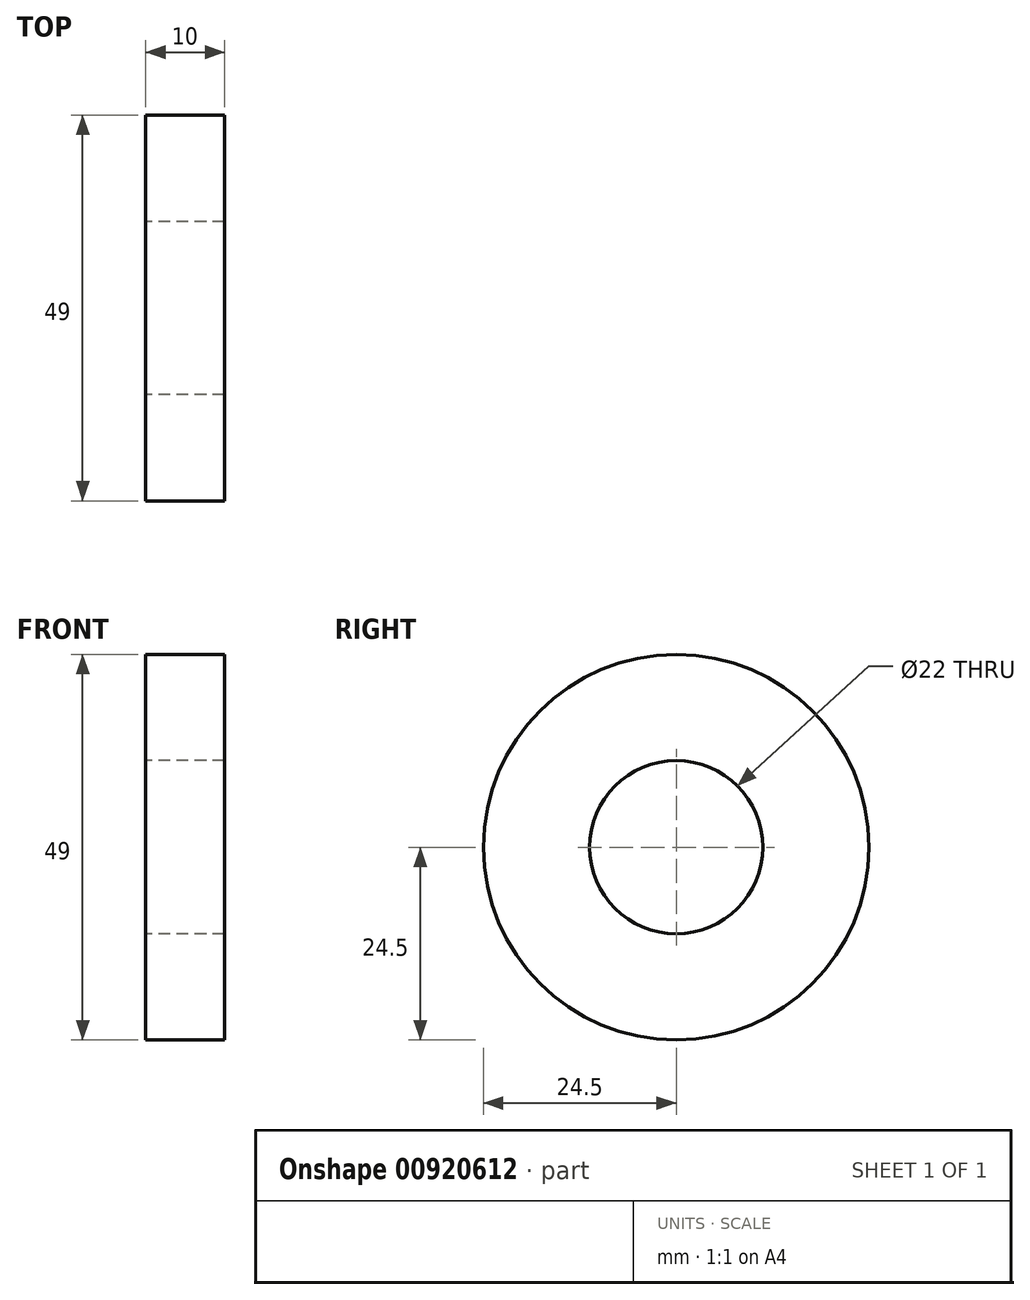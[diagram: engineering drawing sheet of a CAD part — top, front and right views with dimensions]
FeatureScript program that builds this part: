
annotation { "Feature Type Name" : "Feature", "Feature Type Description" : "" }
export const myFeature = defineFeature(function(context is Context, id is Id, definition is map)
    precondition{}
    {
        {
            var Q0;
            Q0=qCreatedBy(makeId("Front.planeOp"),FACE);
            var sketch = newSketch(context, id + "F0", { "sketchPlane" : qUnion([Q0])});
            skLineSegment(sketch, "E0", {"start": v(0, 0) * mm, "end": v(17.92, 0) * mm, "construction": true});
            skLineSegment(sketch, "E1.bottom", {"start": v(0, 11) * mm, "end": v(10, 11) * mm});
            skLineSegment(sketch, "E1.top", {"start": v(0, 24.5) * mm, "end": v(10, 24.5) * mm});
            skLineSegment(sketch, "E1.left", {"start": v(0, 11) * mm, "end": v(0, 24.5) * mm});
            skLineSegment(sketch, "E1.right", {"start": v(10, 11) * mm, "end": v(10, 24.5) * mm});
            skSolve(sketch);
        }
        {
            var Q0;
            Q0=makeQuery(id+"F0.imprint","IMPRINT",FACE,{"disambiguationData":[TD([[makeQuery(id+"F0.imprint","IMPRINT",EDGE,{"derivedFrom":sQuery(id+"F0.wireOp",EDGE,"E1.bottom")}),1.0]])]});
            var Q1;
            Q1=sQuery(id+"F0.wireOp",EDGE,"E0");
            revolve(context, id + "F1", {"surfaceOperationType" : NewSurfaceOperationType.NEW, "entities" : qUnion([Q0]), "axis" : qUnion([Q1]), "revolveType" : RevolveType.FULL});
        }
    });
